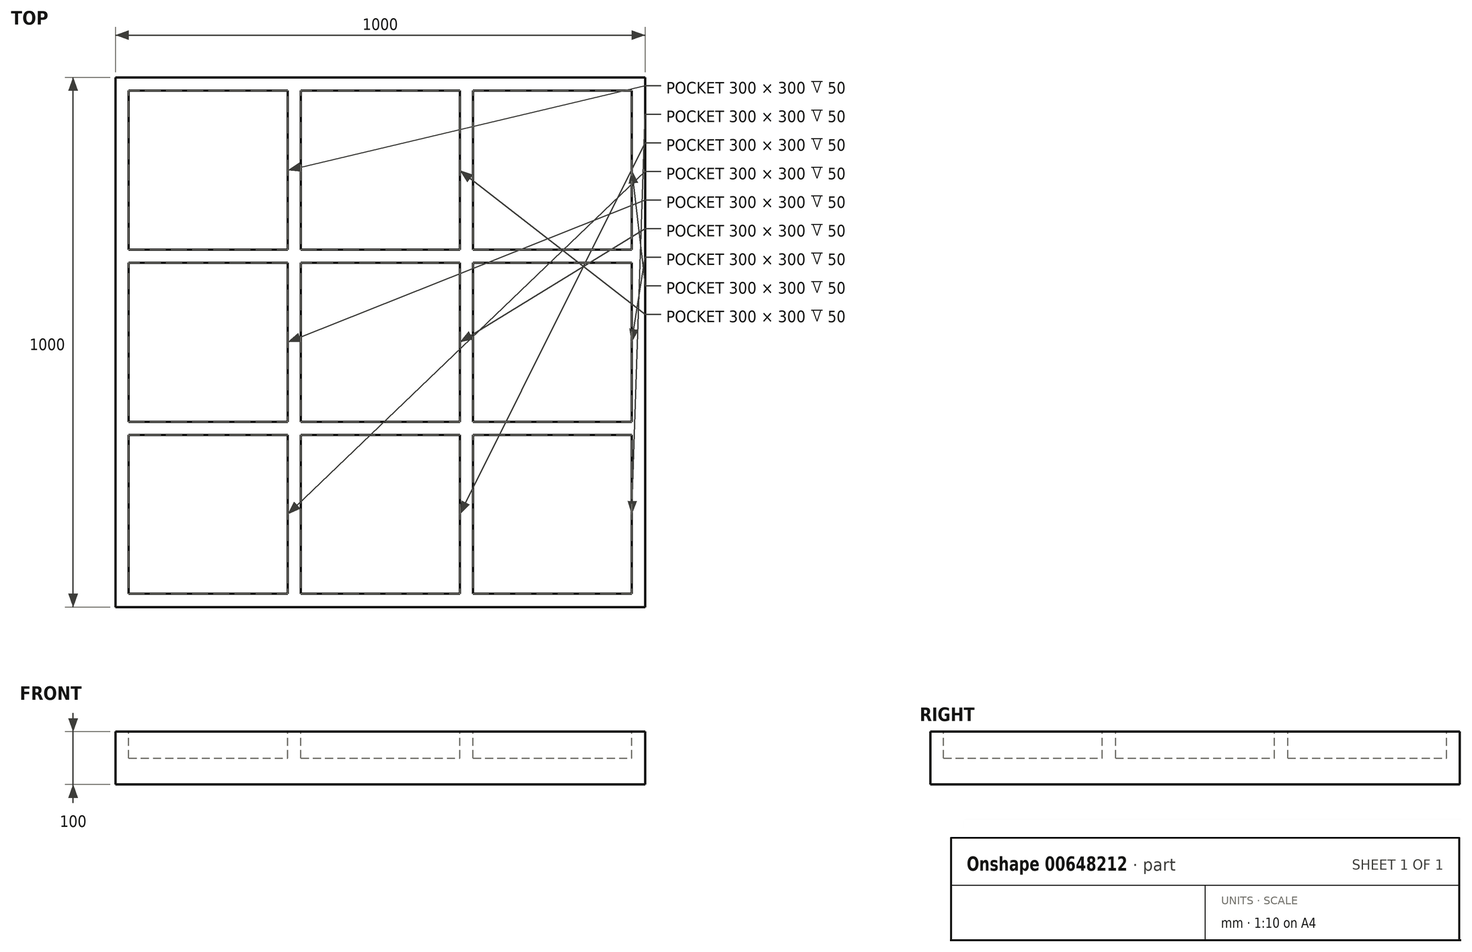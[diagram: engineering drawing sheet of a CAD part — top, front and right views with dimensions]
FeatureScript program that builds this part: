
annotation { "Feature Type Name" : "Feature", "Feature Type Description" : "" }
export const myFeature = defineFeature(function(context is Context, id is Id, definition is map)
    precondition{}
    {
        {
            var Q0;
            Q0=qCreatedBy(makeId("Top.planeOp"),FACE);
            var sketch = newSketch(context, id + "F0", { "sketchPlane" : qUnion([Q0])});
            skLineSegment(sketch, "E0.bottom", {"start": v(500, -500) * mm, "end": v(-500, -500) * mm});
            skLineSegment(sketch, "E0.top", {"start": v(500, 500) * mm, "end": v(-500, 500) * mm});
            skLineSegment(sketch, "E0.left", {"start": v(500, -500) * mm, "end": v(500, 500) * mm});
            skLineSegment(sketch, "E0.right", {"start": v(-500, -500) * mm, "end": v(-500, 500) * mm});
            skPoint(sketch, "E0.middle", {"position": v(0, 0) * mm});
            skSolve(sketch);
        }
        {
            var Q0;
            Q0=makeQuery(id+"F0.imprint","IMPRINT",FACE,{"disambiguationData":[TD([[makeQuery(id+"F0.imprint","IMPRINT",EDGE,{"derivedFrom":sQuery(id+"F0.wireOp",EDGE,"E0.bottom")}),-1.0]])]});
            extrude(context, id + "F1", {"entities" : qUnion([Q0]), "depth" : 100 * mm, "offsetDistance" : 25 * mm});
        }
        {
            var Q0;
            Q0=makeQuery(id+"F1.opExtrude","CAP_FACE",FACE,{"disambiguationData":[OSD([sQuery(id+"F0.wireOp",EDGE,"E0.bottom"),sQuery(id+"F0.wireOp",EDGE,"E0.top"),sQuery(id+"F0.wireOp",EDGE,"E0.left"),sQuery(id+"F0.wireOp",EDGE,"E0.right")])],"isStart":false});
            var sketch = newSketch(context, id + "F2", { "sketchPlane" : qUnion([Q0])});
            skLineSegment(sketch, "E1.bottom", {"start": v(-475, -475) * mm, "end": v(-175, -475) * mm});
            skLineSegment(sketch, "E1.top", {"start": v(-475, -175) * mm, "end": v(-175, -175) * mm});
            skLineSegment(sketch, "E1.left", {"start": v(-475, -475) * mm, "end": v(-475, -175) * mm});
            skLineSegment(sketch, "E1.right", {"start": v(-175, -475) * mm, "end": v(-175, -175) * mm});
            skLineSegment(sketch, "E2.0.1.0", {"start": v(-475, 150) * mm, "end": v(-175, 150) * mm});
            skLineSegment(sketch, "E2.0.1.1", {"start": v(-175, -150) * mm, "end": v(-175, 150) * mm});
            skLineSegment(sketch, "E2.0.1.2", {"start": v(-475, -150) * mm, "end": v(-475, 150) * mm});
            skLineSegment(sketch, "E2.0.1.3", {"start": v(-475, -150) * mm, "end": v(-175, -150) * mm});
            skLineSegment(sketch, "E2.0.2.0", {"start": v(-475, 475) * mm, "end": v(-175, 475) * mm});
            skLineSegment(sketch, "E2.0.2.1", {"start": v(-175, 175) * mm, "end": v(-175, 475) * mm});
            skLineSegment(sketch, "E2.0.2.2", {"start": v(-475, 175) * mm, "end": v(-475, 475) * mm});
            skLineSegment(sketch, "E2.0.2.3", {"start": v(-475, 175) * mm, "end": v(-175, 175) * mm});
            skLineSegment(sketch, "E2.1.0.0", {"start": v(-150, -175) * mm, "end": v(150, -175) * mm});
            skLineSegment(sketch, "E2.1.0.1", {"start": v(150, -475) * mm, "end": v(150, -175) * mm});
            skLineSegment(sketch, "E2.1.0.2", {"start": v(-150, -475) * mm, "end": v(-150, -175) * mm});
            skLineSegment(sketch, "E2.1.0.3", {"start": v(-150, -475) * mm, "end": v(150, -475) * mm});
            skLineSegment(sketch, "E2.1.1.0", {"start": v(-150, 150) * mm, "end": v(150, 150) * mm});
            skLineSegment(sketch, "E2.1.1.1", {"start": v(150, -150) * mm, "end": v(150, 150) * mm});
            skLineSegment(sketch, "E2.1.1.2", {"start": v(-150, -150) * mm, "end": v(-150, 150) * mm});
            skLineSegment(sketch, "E2.1.1.3", {"start": v(-150, -150) * mm, "end": v(150, -150) * mm});
            skLineSegment(sketch, "E2.1.2.0", {"start": v(-150, 475) * mm, "end": v(150, 475) * mm});
            skLineSegment(sketch, "E2.1.2.1", {"start": v(150, 175) * mm, "end": v(150, 475) * mm});
            skLineSegment(sketch, "E2.1.2.2", {"start": v(-150, 175) * mm, "end": v(-150, 475) * mm});
            skLineSegment(sketch, "E2.1.2.3", {"start": v(-150, 175) * mm, "end": v(150, 175) * mm});
            skLineSegment(sketch, "E2.2.0.0", {"start": v(175, -175) * mm, "end": v(475, -175) * mm});
            skLineSegment(sketch, "E2.2.0.1", {"start": v(475, -475) * mm, "end": v(475, -175) * mm});
            skLineSegment(sketch, "E2.2.0.2", {"start": v(175, -475) * mm, "end": v(175, -175) * mm});
            skLineSegment(sketch, "E2.2.0.3", {"start": v(175, -475) * mm, "end": v(475, -475) * mm});
            skLineSegment(sketch, "E2.2.1.0", {"start": v(175, 150) * mm, "end": v(475, 150) * mm});
            skLineSegment(sketch, "E2.2.1.1", {"start": v(475, -150) * mm, "end": v(475, 150) * mm});
            skLineSegment(sketch, "E2.2.1.2", {"start": v(175, -150) * mm, "end": v(175, 150) * mm});
            skLineSegment(sketch, "E2.2.1.3", {"start": v(175, -150) * mm, "end": v(475, -150) * mm});
            skLineSegment(sketch, "E2.2.2.0", {"start": v(175, 475) * mm, "end": v(475, 475) * mm});
            skLineSegment(sketch, "E2.2.2.1", {"start": v(475, 175) * mm, "end": v(475, 475) * mm});
            skLineSegment(sketch, "E2.2.2.2", {"start": v(175, 175) * mm, "end": v(175, 475) * mm});
            skLineSegment(sketch, "E2.2.2.3", {"start": v(175, 175) * mm, "end": v(475, 175) * mm});
            skLineSegment(sketch, "E2.direction1", {"start": v(-450, -200) * mm, "end": v(-125, -200) * mm, "construction": true});
            skLineSegment(sketch, "E2.direction2", {"start": v(-450, -200) * mm, "end": v(-450, 125) * mm, "construction": true});
            skSolve(sketch);
        }
        {
            var Q0;
            Q0=makeQuery(id+"F2.imprint","IMPRINT",FACE,{"disambiguationData":[TD([[makeQuery(id+"F2.imprint","IMPRINT",EDGE,{"derivedFrom":sQuery(id+"F2.wireOp",EDGE,"E2.0.2.0")}),-1.0]])]});
            var Q1;
            Q1=makeQuery(id+"F2.imprint","IMPRINT",FACE,{"disambiguationData":[TD([[makeQuery(id+"F2.imprint","IMPRINT",EDGE,{"derivedFrom":sQuery(id+"F2.wireOp",EDGE,"E2.1.2.0")}),-1.0]])]});
            var Q2;
            Q2=makeQuery(id+"F2.imprint","IMPRINT",FACE,{"disambiguationData":[TD([[makeQuery(id+"F2.imprint","IMPRINT",EDGE,{"derivedFrom":sQuery(id+"F2.wireOp",EDGE,"E2.2.2.0")}),-1.0]])]});
            var Q3;
            Q3=makeQuery(id+"F2.imprint","IMPRINT",FACE,{"disambiguationData":[TD([[makeQuery(id+"F2.imprint","IMPRINT",EDGE,{"derivedFrom":sQuery(id+"F2.wireOp",EDGE,"E2.2.1.0")}),-1.0]])]});
            var Q4;
            Q4=makeQuery(id+"F2.imprint","IMPRINT",FACE,{"disambiguationData":[TD([[makeQuery(id+"F2.imprint","IMPRINT",EDGE,{"derivedFrom":sQuery(id+"F2.wireOp",EDGE,"E2.1.1.0")}),-1.0]])]});
            var Q5;
            Q5=makeQuery(id+"F2.imprint","IMPRINT",FACE,{"disambiguationData":[TD([[makeQuery(id+"F2.imprint","IMPRINT",EDGE,{"derivedFrom":sQuery(id+"F2.wireOp",EDGE,"E2.0.1.0")}),-1.0]])]});
            var Q6;
            Q6=makeQuery(id+"F2.imprint","IMPRINT",FACE,{"disambiguationData":[TD([[makeQuery(id+"F2.imprint","IMPRINT",EDGE,{"derivedFrom":sQuery(id+"F2.wireOp",EDGE,"E1.bottom")}),1.0]])]});
            var Q7;
            Q7=makeQuery(id+"F2.imprint","IMPRINT",FACE,{"disambiguationData":[TD([[makeQuery(id+"F2.imprint","IMPRINT",EDGE,{"derivedFrom":sQuery(id+"F2.wireOp",EDGE,"E2.1.0.0")}),-1.0]])]});
            var Q8;
            Q8=makeQuery(id+"F2.imprint","IMPRINT",FACE,{"disambiguationData":[TD([[makeQuery(id+"F2.imprint","IMPRINT",EDGE,{"derivedFrom":sQuery(id+"F2.wireOp",EDGE,"E2.2.0.0")}),-1.0]])]});
            extrude(context, id + "F3", {"entities" : qUnion([Q0, Q1, Q2, Q3, Q4, Q5, Q6, Q7, Q8]), "operationType" : NewBodyOperationType.REMOVE, "oppositeDirection" : true, "depth" : 50 * mm, "offsetDistance" : 25 * mm});
        }
    });
